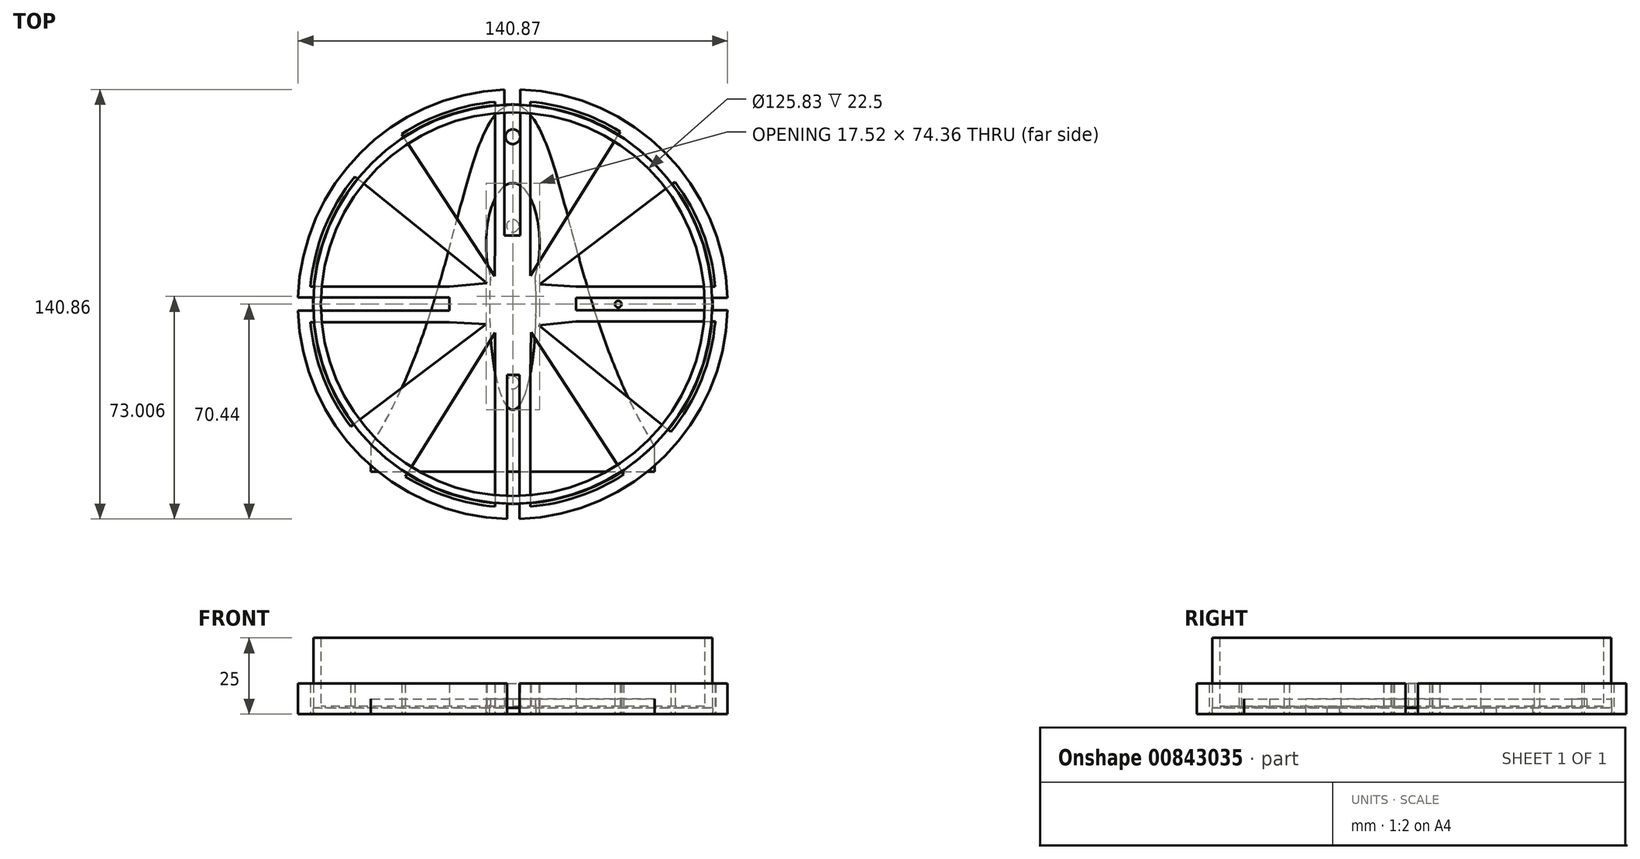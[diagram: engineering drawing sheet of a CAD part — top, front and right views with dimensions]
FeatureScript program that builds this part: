
annotation { "Feature Type Name" : "Feature", "Feature Type Description" : "" }
export const myFeature = defineFeature(function(context is Context, id is Id, definition is map)
    precondition{}
    {
        {
            var Q0;
            Q0=qCreatedBy(makeId("Top.planeOp"),FACE);
            var sketch = newSketch(context, id + "F0", { "sketchPlane" : qUnion([Q0])});
            skCircle(sketch, "E0", {"center": v(0, 0) * mm, "radius": 70.46 * mm});
            skCircle(sketch, "E1", {"center": v(0, 0) * mm, "radius": 66.63 * mm});
            skCircle(sketch, "E2", {"center": v(0, 0) * mm, "radius": 10.95 * mm});
            skLineSegment(sketch, "E3", {"start": v(-1.82, -10.8) * mm, "end": v(-1.82, -66.6) * mm});
            skLineSegment(sketch, "E4", {"start": v(2.18, -10.73) * mm, "end": v(2.18, -66.6) * mm});
            skLineSegment(sketch, "E5", {"start": v(10.78, -1.94) * mm, "end": v(66.6, -1.94) * mm});
            skLineSegment(sketch, "E6", {"start": v(10.76, 2.04) * mm, "end": v(66.6, 2.04) * mm});
            skLineSegment(sketch, "E7", {"start": v(2.48, 10.66) * mm, "end": v(2.48, 66.58) * mm});
            skLineSegment(sketch, "E8", {"start": v(-2.78, 10.59) * mm, "end": v(-2.78, 66.57) * mm});
            skLineSegment(sketch, "E9", {"start": v(-10.73, 2.17) * mm, "end": v(-66.6, 2.17) * mm});
            skLineSegment(sketch, "E10", {"start": v(-10.75, -2.09) * mm, "end": v(-66.6, -2.09) * mm});
            skLineSegment(sketch, "E11", {"start": v(5.8, 9.3) * mm, "end": v(35.24, 56.55) * mm});
            skLineSegment(sketch, "E12", {"start": v(8.74, 6.6) * mm, "end": v(53.2, 40.11) * mm});
            skLineSegment(sketch, "E13", {"start": v(-5.8, -9.3) * mm, "end": v(-35.24, -56.55) * mm});
            skLineSegment(sketch, "E14", {"start": v(-8.74, -6.6) * mm, "end": v(-53.2, -40.11) * mm});
            skLineSegment(sketch, "E15", {"start": v(-8.51, 6.88) * mm, "end": v(-51.82, 41.88) * mm});
            skLineSegment(sketch, "E16", {"start": v(-5.98, 9.17) * mm, "end": v(-36.39, 55.81) * mm});
            skLineSegment(sketch, "E17", {"start": v(5.98, -9.17) * mm, "end": v(36.39, -55.81) * mm});
            skLineSegment(sketch, "E18", {"start": v(8.51, -6.88) * mm, "end": v(51.82, -41.88) * mm});
            skLineSegment(sketch, "E19.bottom", {"start": v(-3.46, -1.94) * mm, "end": v(3.6, -1.94) * mm});
            skLineSegment(sketch, "E19.top", {"start": v(-3.46, 2.04) * mm, "end": v(3.6, 2.04) * mm});
            skLineSegment(sketch, "E19.left", {"start": v(-3.46, -1.94) * mm, "end": v(-3.46, 2.04) * mm});
            skLineSegment(sketch, "E19.right", {"start": v(3.6, -1.94) * mm, "end": v(3.6, 2.04) * mm});
            skCircle(sketch, "E20", {"center": v(34.57, 0) * mm, "radius": 1.09 * mm});
            skLineSegment(sketch, "E21", {"start": v(-2.78, 22.6) * mm, "end": v(2.48, 22.6) * mm});
            skLineSegment(sketch, "E22", {"start": v(5.79, 22.6) * mm, "end": v(5.79, 66.57) * mm});
            skLineSegment(sketch, "E23", {"start": v(-5.79, 66.38) * mm, "end": v(-5.79, 22.6) * mm});
            skLineSegment(sketch, "E24", {"start": v(-5.79, 22.6) * mm, "end": v(-2.78, 22.6) * mm});
            skLineSegment(sketch, "E25", {"start": v(2.48, 22.6) * mm, "end": v(5.79, 22.6) * mm});
            skLineSegment(sketch, "E26", {"start": v(-2.78, 66.57) * mm, "end": v(-2.78, 70.4) * mm});
            skLineSegment(sketch, "E27", {"start": v(2.48, 66.58) * mm, "end": v(2.48, 70.42) * mm});
            skLineSegment(sketch, "E28", {"start": v(5.8, 9.3) * mm, "end": v(5.79, 22.6) * mm});
            skLineSegment(sketch, "E29", {"start": v(-5.79, 22.6) * mm, "end": v(-5.98, 9.17) * mm});
            skLineSegment(sketch, "E30", {"start": v(-1.82, -23.17) * mm, "end": v(2.18, -23.17) * mm});
            skLineSegment(sketch, "E31", {"start": v(2.18, -23.17) * mm, "end": v(5.78, -23.17) * mm});
            skLineSegment(sketch, "E32", {"start": v(5.78, -23.17) * mm, "end": v(5.78, -66.38) * mm});
            skLineSegment(sketch, "E33", {"start": v(-1.82, -23.17) * mm, "end": v(-5.78, -23.17) * mm});
            skLineSegment(sketch, "E34", {"start": v(-5.78, -23.17) * mm, "end": v(-5.78, -66.38) * mm});
            skLineSegment(sketch, "E35", {"start": v(-5.78, -23.17) * mm, "end": v(-5.8, -9.3) * mm});
            skLineSegment(sketch, "E36", {"start": v(5.78, -23.17) * mm, "end": v(5.98, -9.17) * mm});
            skLineSegment(sketch, "E37", {"start": v(20.67, -1.94) * mm, "end": v(20.67, 2.04) * mm});
            skLineSegment(sketch, "E38", {"start": v(20.67, 2.04) * mm, "end": v(20.67, 5.82) * mm});
            skLineSegment(sketch, "E39", {"start": v(20.67, 5.82) * mm, "end": v(66.37, 5.83) * mm});
            skLineSegment(sketch, "E40", {"start": v(20.67, -1.94) * mm, "end": v(20.67, -5.63) * mm});
            skLineSegment(sketch, "E41", {"start": v(20.67, -5.63) * mm, "end": v(66.4, -5.63) * mm});
            skLineSegment(sketch, "E42", {"start": v(-20.77, 2.17) * mm, "end": v(-20.77, -2.09) * mm});
            skLineSegment(sketch, "E43", {"start": v(-20.77, -2.09) * mm, "end": v(-20.77, -5.91) * mm});
            skLineSegment(sketch, "E44", {"start": v(-20.77, -5.91) * mm, "end": v(-66.37, -5.91) * mm});
            skLineSegment(sketch, "E45", {"start": v(-20.77, 2.17) * mm, "end": v(-20.77, 5.82) * mm});
            skLineSegment(sketch, "E46", {"start": v(-20.77, 5.82) * mm, "end": v(-66.37, 5.82) * mm});
            skLineSegment(sketch, "E47", {"start": v(-20.77, -5.91) * mm, "end": v(-8.74, -6.6) * mm});
            skLineSegment(sketch, "E48", {"start": v(-20.77, 5.82) * mm, "end": v(-8.51, 6.88) * mm});
            skLineSegment(sketch, "E49", {"start": v(8.74, 6.6) * mm, "end": v(20.67, 5.82) * mm});
            skLineSegment(sketch, "E50", {"start": v(20.67, -5.63) * mm, "end": v(8.51, -6.88) * mm});
            skLineSegment(sketch, "E51", {"start": v(66.6, -1.94) * mm, "end": v(70.44, -2) * mm});
            skLineSegment(sketch, "E52", {"start": v(66.6, 2.04) * mm, "end": v(70.43, 2.04) * mm});
            skLineSegment(sketch, "E53", {"start": v(-66.6, -2.09) * mm, "end": v(-70.43, -2.09) * mm});
            skLineSegment(sketch, "E54", {"start": v(-70.43, 2.17) * mm, "end": v(-66.6, 2.17) * mm});
            skLineSegment(sketch, "E55", {"start": v(-1.82, -66.6) * mm, "end": v(-1.82, -70.44) * mm});
            skLineSegment(sketch, "E56", {"start": v(2.18, -66.6) * mm, "end": v(2.18, -70.43) * mm});
            skSolve(sketch);
        }
        {
            var Q0;
            Q0=qCreatedBy(makeId("Top.planeOp"),FACE);
            var sketch = newSketch(context, id + "F1", { "sketchPlane" : qUnion([Q0])});
            skCircle(sketch, "E57", {"center": v(0, 0) * mm, "radius": 65.42 * mm});
            skSolve(sketch);
        }
        {
            var Q0;
            Q0 = qSketchRegion(id + "F1", true);
            extrude(context, id + "F2", {"entities" : qUnion([Q0]), "depth" : 25 * mm, "offsetDistance" : 25 * mm});
        }
        {
            var Q0;
            Q0=makeQuery(id+"F2.opExtrude","CAP_FACE",FACE,{"disambiguationData":[OSD([sQuery(id+"F1.wireOp",EDGE,"E57")])],"isStart":false});
            shell(context, id + "F3", {"entities" : qUnion([Q0]), "thickness" : 2.5 * mm});
        }
        {
            var Q0;
            Q0=qCreatedBy(makeId("Top.planeOp"),FACE);
            var sketch = newSketch(context, id + "F4", { "sketchPlane" : qUnion([Q0])});
            skCircle(sketch, "E58", {"center": v(0, 0) * mm, "radius": 65.51 * mm});
            skCircle(sketch, "E59", {"center": v(0, 25.72) * mm, "radius": 2.05 * mm});
            skCircle(sketch, "E60.MirrorC", {"center": v(0, -25.72) * mm, "radius": 2.05 * mm});
            skSolve(sketch);
        }
        {
            var Q0;
            Q0=makeQuery(id+"F4.imprint","IMPRINT",FACE,{"disambiguationData":[TD([[makeQuery(id+"F4.imprint","IMPRINT",EDGE,{"derivedFrom":sQuery(id+"F4.wireOp",EDGE,"E58")}),1.0]])]});
            extrude(context, id + "F5", {"entities" : qUnion([Q0]), "depth" : 2 * mm, "offsetDistance" : 25 * mm});
        }
        {
            var Q0;
            Q0=qCreatedBy(makeId("Top.planeOp"),FACE);
            var sketch = newSketch(context, id + "F6", { "sketchPlane" : qUnion([Q0])});
            skLineSegment(sketch, "E61", {"start": v(-46.56, -46.56) * mm, "end": v(46.56, -46.56) * mm});
            skLineSegment(sketch, "E62", {"start": v(0, -46.56) * mm, "end": v(0, 65.6) * mm});
            skPoint(sketch, "E62.endSnap0", {"position": v(0, -46.56) * mm});
            skFitSpline(sketch, "E63", {"points": [v(-46.56, -46.56) * mm, v(0, 65.6) * mm], "startDerivative": vector(87.78, 139.68) * mm, "endDerivative": vector(51.22, 5.04) * mm});
            skFitSpline(sketch, "E64.MirrorCS", {"points": [v(46.56, -46.56) * mm, v(0, 65.6) * mm], "startDerivative": vector(-87.78, 139.68) * mm, "endDerivative": vector(-51.22, 5.04) * mm});
            skEllipse(sketch, "E65", {"center": v(0, 19.87) * mm, "majorRadius": 19.87 * mm, "minorRadius": 8.77 * mm, "majorAxis": v(0, -1)});
            skPoint(sketch, "E66.first.point", {"position": v(0, -15.96) * mm});
            skPoint(sketch, "E66.second.point", {"position": v(0, 9.52) * mm});
            skEllipse(sketch, "E67", {"center": v(0, 0) * mm, "majorRadius": 34.62 * mm, "minorRadius": 7.65 * mm, "majorAxis": v(0, -1)});
            skLineSegment(sketch, "E68", {"start": v(-46.56, -46.56) * mm, "end": v(-46.56, -54.96) * mm});
            skLineSegment(sketch, "E69", {"start": v(-46.56, -54.96) * mm, "end": v(46.56, -54.96) * mm});
            skLineSegment(sketch, "E70", {"start": v(46.56, -54.96) * mm, "end": v(46.56, -46.56) * mm});
            skCircle(sketch, "E71", {"center": v(0, 54.96) * mm, "radius": 2.42 * mm});
            skSolve(sketch);
        }
        {
            var Q0;
            Q0 = qSketchRegion(id + "F6", true);
            extrude(context, id + "F7", {"entities" : qUnion([Q0]), "depth" : 5 * mm, "offsetDistance" : 25 * mm});
        }
        {
            var Q0;
            {var subQ5=sQuery(id+"F0.wireOp",EDGE,"E30");Q0=makeQuery(id+"F0.imprint","IMPRINT",FACE,{"disambiguationData":[TD([[makeQuery(id+"F0.imprint","IMPRINT",EDGE,{"derivedFrom":subQ5}),1.0]])]});}
            var Q1;
            {var subQ4=sQuery(id+"F0.wireOp",EDGE,"E38");Q1=makeQuery(id+"F0.imprint","IMPRINT",FACE,{"disambiguationData":[TD([[makeQuery(id+"F0.imprint","IMPRINT",EDGE,{"derivedFrom":subQ4}),-1.0]])]});}
            var Q2;
            {var subQ0=sQuery(id+"F0.wireOp",EDGE,"E13");Q2=makeQuery(id+"F0.imprint","IMPRINT",FACE,{"disambiguationData":[TD([[makeQuery(id+"F0.imprint","IMPRINT",EDGE,{"derivedFrom":subQ0}),-1.0]])]});}
            var Q3;
            {var subQ4=sQuery(id+"F0.wireOp",EDGE,"E25");Q3=makeQuery(id+"F0.imprint","IMPRINT",FACE,{"disambiguationData":[TD([[makeQuery(id+"F0.imprint","IMPRINT",EDGE,{"derivedFrom":subQ4}),-1.0]])]});}
            var Q4;
            {var subQ4=sQuery(id+"F0.wireOp",EDGE,"E31");Q4=makeQuery(id+"F0.imprint","IMPRINT",FACE,{"disambiguationData":[TD([[makeQuery(id+"F0.imprint","IMPRINT",EDGE,{"derivedFrom":subQ4}),-1.0]])]});}
            var Q5;
            {var subQ4=sQuery(id+"F0.wireOp",EDGE,"E24");Q5=makeQuery(id+"F0.imprint","IMPRINT",FACE,{"disambiguationData":[TD([[makeQuery(id+"F0.imprint","IMPRINT",EDGE,{"derivedFrom":subQ4}),-1.0]])]});}
            var Q6;
            {var subQ4=sQuery(id+"F0.wireOp",EDGE,"E31");Q6=makeQuery(id+"F0.imprint","IMPRINT",FACE,{"disambiguationData":[TD([[makeQuery(id+"F0.imprint","IMPRINT",EDGE,{"derivedFrom":subQ4}),1.0]])]});}
            var Q7;
            {var subQ0=sQuery(id+"F0.wireOp",EDGE,"E15");Q7=makeQuery(id+"F0.imprint","IMPRINT",FACE,{"disambiguationData":[TD([[makeQuery(id+"F0.imprint","IMPRINT",EDGE,{"derivedFrom":subQ0}),-1.0]])]});}
            var Q8;
            {var subQ4=sQuery(id+"F0.wireOp",EDGE,"E33");Q8=makeQuery(id+"F0.imprint","IMPRINT",FACE,{"disambiguationData":[TD([[makeQuery(id+"F0.imprint","IMPRINT",EDGE,{"derivedFrom":subQ4}),1.0]])]});}
            var Q9;
            {var subQ4=sQuery(id+"F0.wireOp",EDGE,"E45");Q9=makeQuery(id+"F0.imprint","IMPRINT",FACE,{"disambiguationData":[TD([[makeQuery(id+"F0.imprint","IMPRINT",EDGE,{"derivedFrom":subQ4}),1.0]])]});}
            var Q10;
            {var subQ0=sQuery(id+"F0.wireOp",EDGE,"E17");Q10=makeQuery(id+"F0.imprint","IMPRINT",FACE,{"disambiguationData":[TD([[makeQuery(id+"F0.imprint","IMPRINT",EDGE,{"derivedFrom":subQ0}),1.0]])]});}
            var Q11;
            {var subQ4=sQuery(id+"F0.wireOp",EDGE,"E33");Q11=makeQuery(id+"F0.imprint","IMPRINT",FACE,{"disambiguationData":[TD([[makeQuery(id+"F0.imprint","IMPRINT",EDGE,{"derivedFrom":subQ4}),-1.0]])]});}
            var Q12;
            {var subQ4=sQuery(id+"F0.wireOp",EDGE,"E45");Q12=makeQuery(id+"F0.imprint","IMPRINT",FACE,{"disambiguationData":[TD([[makeQuery(id+"F0.imprint","IMPRINT",EDGE,{"derivedFrom":subQ4}),-1.0]])]});}
            var Q13;
            {var subQ5=sQuery(id+"F0.wireOp",EDGE,"E37");Q13=makeQuery(id+"F0.imprint","IMPRINT",FACE,{"disambiguationData":[TD([[makeQuery(id+"F0.imprint","IMPRINT",EDGE,{"derivedFrom":subQ5}),1.0]])]});}
            var Q14;
            {var subQ3=sQuery(id+"F0.wireOp",EDGE,"E51");Q14=makeQuery(id+"F0.imprint","IMPRINT",FACE,{"disambiguationData":[TD([[makeQuery(id+"F0.imprint","IMPRINT",EDGE,{"derivedFrom":subQ3}),-1.0]])]});}
            var Q15;
            {var subQ3=sQuery(id+"F0.wireOp",EDGE,"E26");Q15=makeQuery(id+"F0.imprint","IMPRINT",FACE,{"disambiguationData":[TD([[makeQuery(id+"F0.imprint","IMPRINT",EDGE,{"derivedFrom":subQ3}),1.0]])]});}
            var Q16;
            {var subQ0=sQuery(id+"F0.wireOp",EDGE,"E11");Q16=makeQuery(id+"F0.imprint","IMPRINT",FACE,{"disambiguationData":[TD([[makeQuery(id+"F0.imprint","IMPRINT",EDGE,{"derivedFrom":subQ0}),-1.0]])]});}
            var Q17;
            {var subQ5=sQuery(id+"F0.wireOp",EDGE,"E42");Q17=makeQuery(id+"F0.imprint","IMPRINT",FACE,{"disambiguationData":[TD([[makeQuery(id+"F0.imprint","IMPRINT",EDGE,{"derivedFrom":subQ5}),1.0]])]});}
            var Q18;
            Q18=makeQuery(id+"F0.imprint","IMPRINT",FACE,{"disambiguationData":[TD([[makeQuery(id+"F0.imprint","IMPRINT",EDGE,{"derivedFrom":sQuery(id+"F0.wireOp",EDGE,"E19.bottom")}),-1.0]])]});
            var Q19;
            {var subQ4=sQuery(id+"F0.wireOp",EDGE,"E38");Q19=makeQuery(id+"F0.imprint","IMPRINT",FACE,{"disambiguationData":[TD([[makeQuery(id+"F0.imprint","IMPRINT",EDGE,{"derivedFrom":subQ4}),1.0]])]});}
            var Q20;
            {var subQ5=sQuery(id+"F0.wireOp",EDGE,"E21");Q20=makeQuery(id+"F0.imprint","IMPRINT",FACE,{"disambiguationData":[TD([[makeQuery(id+"F0.imprint","IMPRINT",EDGE,{"derivedFrom":subQ5}),-1.0]])]});}
            var Q21;
            {var subQ4=sQuery(id+"F0.wireOp",EDGE,"E53");Q21=makeQuery(id+"F0.imprint","IMPRINT",FACE,{"disambiguationData":[TD([[makeQuery(id+"F0.imprint","IMPRINT",EDGE,{"derivedFrom":subQ4}),1.0]])]});}
            var Q22;
            {var subQ5=sQuery(id+"F0.wireOp",EDGE,"E25");Q22=makeQuery(id+"F0.imprint","IMPRINT",FACE,{"disambiguationData":[TD([[makeQuery(id+"F0.imprint","IMPRINT",EDGE,{"derivedFrom":subQ5}),1.0]])]});}
            var Q23;
            {var subQ5=sQuery(id+"F0.wireOp",EDGE,"E27");Q23=makeQuery(id+"F0.imprint","IMPRINT",FACE,{"disambiguationData":[TD([[makeQuery(id+"F0.imprint","IMPRINT",EDGE,{"derivedFrom":subQ5}),-1.0]])]});}
            var Q24;
            {var subQ3=sQuery(id+"F0.wireOp",EDGE,"E23");Q24=makeQuery(id+"F0.imprint","IMPRINT",FACE,{"disambiguationData":[TD([[makeQuery(id+"F0.imprint","IMPRINT",EDGE,{"derivedFrom":subQ3}),1.0]])]});}
            var Q25;
            Q25=makeQuery(id+"F0.imprint","IMPRINT",FACE,{"disambiguationData":[TD([[makeQuery(id+"F0.imprint","IMPRINT",EDGE,{"derivedFrom":sQuery(id+"F0.wireOp",EDGE,"E19.bottom")}),1.0]])]});
            var Q26;
            {var subQ4=sQuery(id+"F0.wireOp",EDGE,"E43");Q26=makeQuery(id+"F0.imprint","IMPRINT",FACE,{"disambiguationData":[TD([[makeQuery(id+"F0.imprint","IMPRINT",EDGE,{"derivedFrom":subQ4}),-1.0]])]});}
            var Q27;
            {var subQ4=sQuery(id+"F0.wireOp",EDGE,"E40");Q27=makeQuery(id+"F0.imprint","IMPRINT",FACE,{"disambiguationData":[TD([[makeQuery(id+"F0.imprint","IMPRINT",EDGE,{"derivedFrom":subQ4}),1.0]])]});}
            var Q28;
            {var subQ4=sQuery(id+"F0.wireOp",EDGE,"E43");Q28=makeQuery(id+"F0.imprint","IMPRINT",FACE,{"disambiguationData":[TD([[makeQuery(id+"F0.imprint","IMPRINT",EDGE,{"derivedFrom":subQ4}),1.0]])]});}
            var Q29;
            {var subQ4=sQuery(id+"F0.wireOp",EDGE,"E40");Q29=makeQuery(id+"F0.imprint","IMPRINT",FACE,{"disambiguationData":[TD([[makeQuery(id+"F0.imprint","IMPRINT",EDGE,{"derivedFrom":subQ4}),-1.0]])]});}
            var Q30;
            Q30=makeQuery(id+"F0.imprint","IMPRINT",FACE,{"disambiguationData":[TD([[makeQuery(id+"F0.imprint","IMPRINT",EDGE,{"derivedFrom":sQuery(id+"F0.wireOp",EDGE,"E20")}),1.0]])]});
            extrude(context, id + "F8", {"entities" : qUnion([Q0, Q1, Q2, Q3, Q4, Q5, Q6, Q7, Q8, Q9, Q10, Q11, Q12, Q13, Q14, Q15, Q16, Q17, Q18, Q19, Q20, Q21, Q22, Q23, Q24, Q25, Q26, Q27, Q28, Q29, Q30]), "depth" : 10 * mm, "offsetDistance" : 25 * mm});
        }
    });
